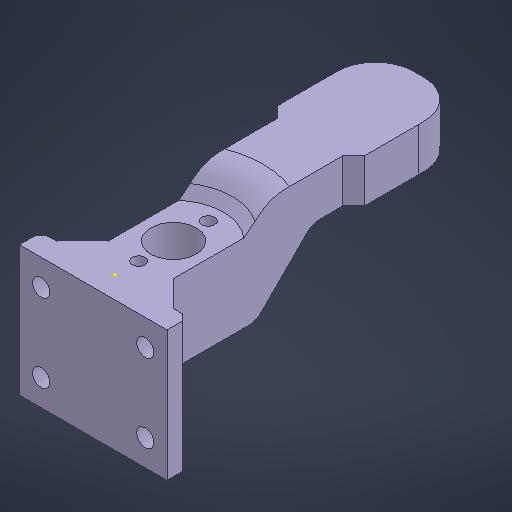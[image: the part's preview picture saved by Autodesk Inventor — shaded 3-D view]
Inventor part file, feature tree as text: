
AUTODESK INVENTOR PART (.ipt)
format: ipt  version: 2025.1 (Build 291241000, 241)  size: 748,544 bytes
history: native  units: in
note: dims shown in document units (in); Inventor stores cm internally (conversion verified against a paired STEP export)
features: extrude x9, chamfer x6, sketch x5, fillet x3, plane x1
ambient origin geometry x8: Origin, YZ Plane, XZ Plane, XY Plane, X Axis, Y Axis, Z Axis, Center Point
bodies: Solid1 (feature_tree)
feature tree (24):
  sketch  "Sketch1"  dims[d0=1.1811in d1=1.3386in]
  extrude  "Extrusion1"  Depth=1.3386in
  sketch  "Sketch2"  dims[d2=0.1575in d3=0.9449in]
  extrude  "Extrusion2"  Depth=0.1575in
  extrude  "Extrusion3"  Depth=0.7087in
  chamfer  "Chamfer2"  Distance=0.2362in
  sketch  "Sketch3"  dims[d4=0.9449in d5=0.7087in]
  extrude  "Extrusion4"  Depth=0.1969in
  fillet  "Fillet7"  Radius=0.1969in
  extrude  "Extrusion5"  Depth=0.1969in TaperAngle=0.0deg
  chamfer  "Chamfer9"  Distance=0.4134in
  fillet  "Fillet10"  Radius=0.1181in
  extrude  "Extrusion6"  Depth=0.3937in
  chamfer  "Chamfer12"  Distance=0.315in
  chamfer  "Chamfer13"  Distance=0.315in
  fillet  "Fillet13"  Radius=0.9055in
  sketch  "Sketch5"  dims[d7=0.1969in d8=0.2362in d9=0.1969in d10=0.1969in d11=0.1969in d12=0.0in d13=0.4134in d14=0.1181in d15=0.1181in d16=0.315in d17=0.315in d18=0.9055in d19=0.7283in d24=0.5906in d25=0.2953in d28=0.1969in d29=0.0in d30=0.2165in d31=0.0in d35=0.1181in d36=0.3937in d37=45.0deg d48=1.7717in d49=0.9843in d50=0.7874in d51=0.3937in d52=0.0in d64=0.3937in d67=0.7087in d68=0.0in d75=0.5118in d76=0.5118in d77=45.0deg d78=0.1969in d83=0.1969in d84=0.0in d89=0.1969in d90=0.0787in d91=45.0deg d92=0.3937in d93=0.0984in d94=0.0787in d95=45.0deg d99=0.2283in d100=0.2283in d101=0.2283in d102=0.2283in d103=-0.3937in d104=0.1181in d105=0.0in d106=0.0591in d107=0.0787in d108=45.0deg d109=0.315in d110=0.315in d111=0.315in d112=0.315in d113=0.2362in d114=0.0787in d115=45.0deg d116=0.0in d117=0.0in d118=0.3937in d119=0.0in d69=0.0197in d70=0.0344in]
  plane  "Work Plane1"
  extrude  "Extrusion7"  Depth=0.3937in
  chamfer  "Chamfer15"  Distance=0.5906in
  chamfer  "Chamfer16"  Distance=0.2953in
  extrude  "Extrusion8"  Depth=0.1969in TaperAngle=0.0deg
  extrude  "Extrusion9"  Depth=0.3937in TaperAngle=0.0deg
  sketch  "Sketch4"  dims[d6=0.7087in]
